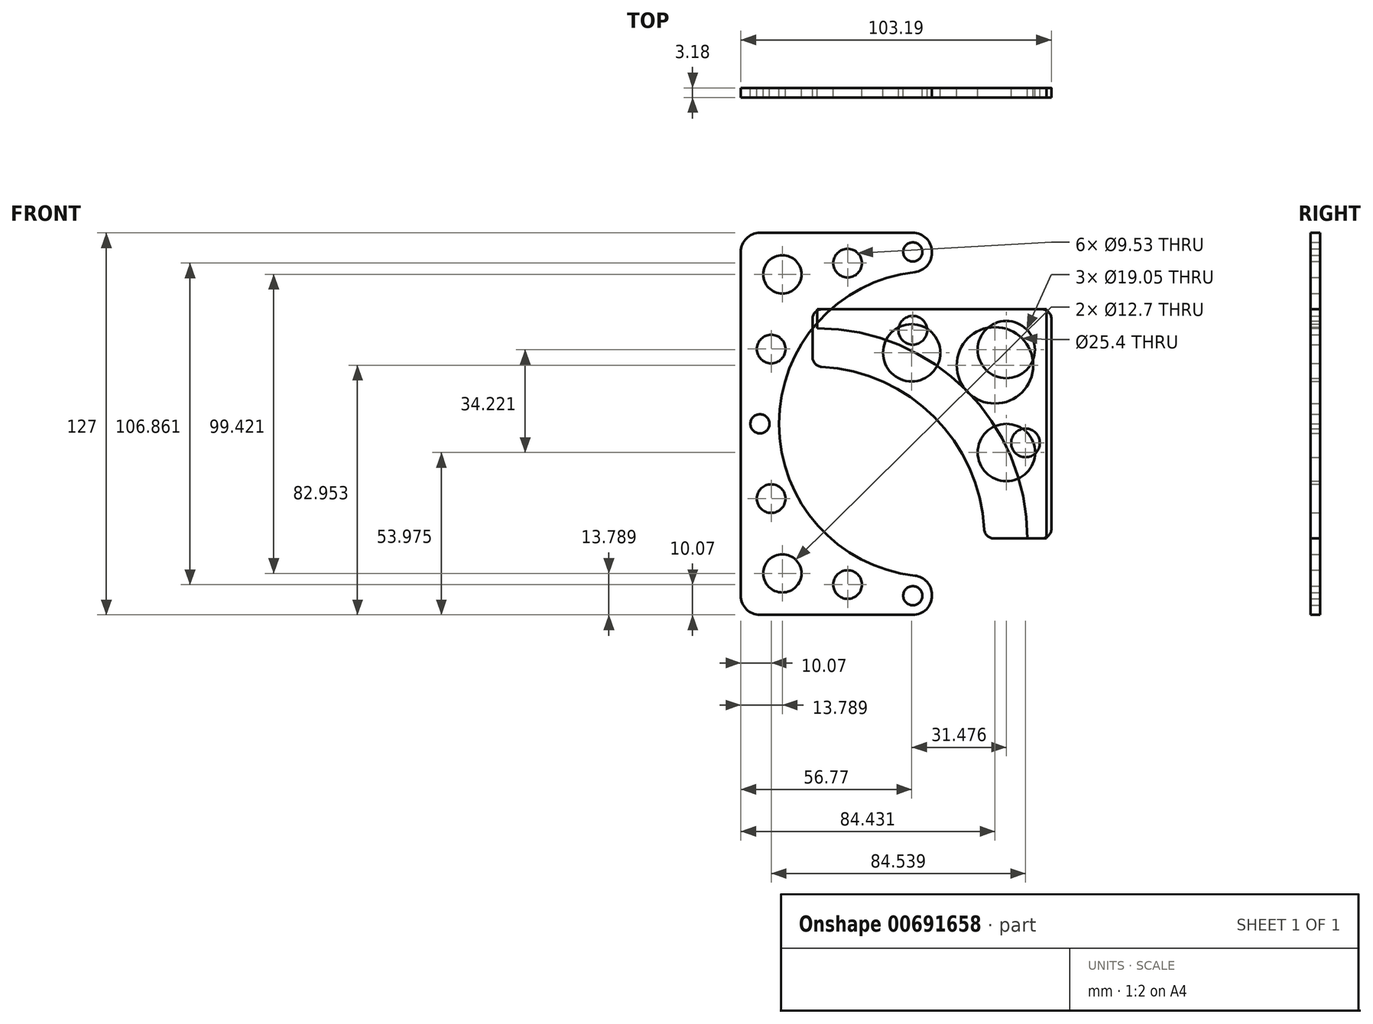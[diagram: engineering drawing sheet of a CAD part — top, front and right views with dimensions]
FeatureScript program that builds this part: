
annotation { "Feature Type Name" : "Feature", "Feature Type Description" : "" }
export const myFeature = defineFeature(function(context is Context, id is Id, definition is map)
    precondition{}
    {
        {
            var Q0;
            Q0=qCreatedBy(makeId("Front.planeOp"),FACE);
            var sketch = newSketch(context, id + "F0", { "sketchPlane" : qUnion([Q0])});
            skLineSegment(sketch, "E0.bottom", {"start": v(38.1, 38.1) * mm, "end": v(-38.1, 38.1) * mm});
            skLineSegment(sketch, "E0.top", {"start": v(38.1, -38.1) * mm, "end": v(31.75, -38.1) * mm});
            skLineSegment(sketch, "E0.left", {"start": v(38.1, 38.1) * mm, "end": v(38.1, -38.1) * mm});
            skLineSegment(sketch, "E0.right", {"start": v(-38.1, 38.1) * mm, "end": v(-38.1, 31.75) * mm});
            skPoint(sketch, "E0.middle", {"position": v(0, 0) * mm});
            skArc(sketch, "E1", {"start": v(31.75, -38.1) * mm, "mid": v(11.3, 11.3) * mm, "end": v(-38.1, 31.75) * mm});
            skCircle(sketch, "E2", {"center": v(24.7, 24.7) * mm, "radius": 9.53 * mm});
            skPoint(sketch, "E3.trimOffspring.end.orphan", {"position": v(11.3, 11.3) * mm});
            skCircle(sketch, "E4", {"center": v(31.1, -6.35) * mm, "radius": 4.76 * mm});
            skPoint(sketch, "E5.trimOffspring.end.orphan", {"position": v(24.12, -6.35) * mm});
            skPoint(sketch, "E6.start.orphan", {"position": v(38.1, -6.35) * mm});
            skLineSegment(sketch, "E7", {"start": v(-38.1, 38.1) * mm, "end": v(-6.35, 38.1) * mm});
            skLineSegment(sketch, "E8", {"start": v(-6.35, 38.1) * mm, "end": v(-6.35, 24.12) * mm});
            skCircle(sketch, "E9", {"center": v(-6.35, 31.1) * mm, "radius": 4.76 * mm});
            skSolve(sketch);
        }
        {
            var Q0;
            Q0 = qSketchRegion(id + "F0", true);
            extrude(context, id + "F1", {"entities" : qUnion([Q0]), "depth" : 3.17 * mm, "offsetDistance" : 25.4 * mm});
        }
        {
            var Q0;
            Q0=qCreatedBy(makeId("Front.planeOp"),FACE);
            var sketch = newSketch(context, id + "F2", { "sketchPlane" : qUnion([Q0])});
            skLineSegment(sketch, "E10.bottom", {"start": v(36.51, 38.1) * mm, "end": v(-36.51, 38.1) * mm});
            skLineSegment(sketch, "E10.top", {"start": v(36.51, -38.1) * mm, "end": v(20.55, -38.1) * mm});
            skLineSegment(sketch, "E10.left", {"start": v(39.69, 34.93) * mm, "end": v(39.69, -34.93) * mm});
            skLineSegment(sketch, "E10.right", {"start": v(-39.69, 34.93) * mm, "end": v(-39.69, 22.14) * mm});
            skPoint(sketch, "E10.middle", {"position": v(0, 0) * mm});
            skArc(sketch, "E11", {"start": v(17.38, -35.1) * mm, "mid": v(0.72, 2.31) * mm, "end": v(-36.68, 18.97) * mm});
            skCircle(sketch, "E12", {"center": v(24.75, -9.53) * mm, "radius": 9.53 * mm});
            skPoint(sketch, "E13.trimOffspring.end.orphan", {"position": v(9.8, -9.53) * mm});
            skPoint(sketch, "E14.end.orphan", {"position": v(39.69, -9.53) * mm});
            skCircle(sketch, "E15", {"center": v(-6.73, 23.6) * mm, "radius": 9.53 * mm});
            skPoint(sketch, "E16.trimOffspring.end.orphan", {"position": v(-7.49, 9.12) * mm});
            skPoint(sketch, "E17.end.orphan", {"position": v(-5.97, 38.1) * mm});
            skCircle(sketch, "E18", {"center": v(20.93, 19.45) * mm, "radius": 12.7 * mm});
            skPoint(sketch, "E19.trimOffspring.end.orphan", {"position": v(2.17, 0.8) * mm});
            skPoint(sketch, "E20.visualSharp", {"position": v(39.69, 38.1) * mm});
            skArc(sketch, "E20.filletArc", {"start": v(39.69, 34.93) * mm, "mid": v(38.76, 37.17) * mm, "end": v(36.51, 38.1) * mm});
            skPoint(sketch, "E21.visualSharp", {"position": v(39.69, -38.1) * mm});
            skArc(sketch, "E21.filletArc", {"start": v(36.51, -38.1) * mm, "mid": v(38.76, -37.17) * mm, "end": v(39.69, -34.93) * mm});
            skPoint(sketch, "E22.visualSharp", {"position": v(17.46, -38.1) * mm});
            skArc(sketch, "E22.filletArc", {"start": v(17.38, -35.1) * mm, "mid": v(18.37, -37.23) * mm, "end": v(20.55, -38.1) * mm});
            skPoint(sketch, "E23.visualSharp", {"position": v(-39.69, 19.05) * mm});
            skArc(sketch, "E23.filletArc", {"start": v(-39.69, 22.14) * mm, "mid": v(-38.82, 19.96) * mm, "end": v(-36.68, 18.97) * mm});
            skPoint(sketch, "E24.visualSharp", {"position": v(-39.69, 38.1) * mm});
            skArc(sketch, "E24.filletArc", {"start": v(-36.51, 38.1) * mm, "mid": v(-38.76, 37.17) * mm, "end": v(-39.69, 34.93) * mm});
            skSolve(sketch);
        }
        {
            var Q0;
            Q0 = qSketchRegion(id + "F2", true);
            extrude(context, id + "F3", {"entities" : qUnion([Q0]), "depth" : 3.17 * mm, "offsetDistance" : 25.4 * mm});
        }
        {
            var Q0;
            Q0=qCreatedBy(makeId("Front.planeOp"),FACE);
            var sketch = newSketch(context, id + "F4", { "sketchPlane" : qUnion([Q0])});
            skLineSegment(sketch, "E25.bottom", {"start": v(-6.35, 63.5) * mm, "end": v(-57.15, 63.5) * mm});
            skLineSegment(sketch, "E25.top", {"start": v(-6.35, -63.5) * mm, "end": v(-57.15, -63.5) * mm});
            skLineSegment(sketch, "E25.right", {"start": v(-63.5, 57.15) * mm, "end": v(-63.5, -57.15) * mm});
            skPoint(sketch, "E25.middle", {"position": v(0, 0) * mm});
            skArc(sketch, "E26", {"start": v(-5.64, 50.49) * mm, "mid": v(-50.8, 0) * mm, "end": v(-5.64, -50.49) * mm});
            skLineSegment(sketch, "E27", {"start": v(0, 57.15) * mm, "end": v(0, 56.8) * mm});
            skPoint(sketch, "E28.orphan", {"position": v(63.5, -63.5) * mm});
            skPoint(sketch, "E25.left.end.orphan", {"position": v(63.5, 0) * mm});
            skPoint(sketch, "E29.orphan", {"position": v(63.5, 63.5) * mm});
            skLineSegment(sketch, "E30.trimOffspring", {"start": v(0, -56.8) * mm, "end": v(0, -57.15) * mm});
            skPoint(sketch, "E31.visualSharp", {"position": v(0, 63.5) * mm});
            skArc(sketch, "E31.filletArc", {"start": v(0, 57.15) * mm, "mid": v(-1.86, 61.64) * mm, "end": v(-6.35, 63.5) * mm});
            skPoint(sketch, "E32.visualSharp", {"position": v(0, 50.8) * mm});
            skArc(sketch, "E32.filletArc", {"start": v(-5.64, 50.49) * mm, "mid": v(-1.62, 52.56) * mm, "end": v(0, 56.8) * mm});
            skPoint(sketch, "E33.visualSharp", {"position": v(-63.5, 63.5) * mm});
            skArc(sketch, "E33.filletArc", {"start": v(-57.15, 63.5) * mm, "mid": v(-61.64, 61.64) * mm, "end": v(-63.5, 57.15) * mm});
            skPoint(sketch, "E34.visualSharp", {"position": v(0, -50.8) * mm});
            skArc(sketch, "E34.filletArc", {"start": v(0, -56.8) * mm, "mid": v(-1.62, -52.56) * mm, "end": v(-5.64, -50.49) * mm});
            skPoint(sketch, "E35.visualSharp", {"position": v(0, -63.5) * mm});
            skArc(sketch, "E35.filletArc", {"start": v(-6.35, -63.5) * mm, "mid": v(-1.86, -61.64) * mm, "end": v(0, -57.15) * mm});
            skPoint(sketch, "E36.visualSharp", {"position": v(-63.5, -63.5) * mm});
            skArc(sketch, "E36.filletArc", {"start": v(-63.5, -57.15) * mm, "mid": v(-61.64, -61.64) * mm, "end": v(-57.15, -63.5) * mm});
            skLineSegment(sketch, "E37", {"start": v(-63.5, 63.5) * mm, "end": v(-61.64, 61.64) * mm});
            skLineSegment(sketch, "E38", {"start": v(-63.5, -63.5) * mm, "end": v(-61.64, -61.64) * mm});
            skCircle(sketch, "E39", {"center": v(-49.71, 49.71) * mm, "radius": 6.35 * mm});
            skCircle(sketch, "E40", {"center": v(-49.71, -49.71) * mm, "radius": 6.35 * mm});
            skPoint(sketch, "E41.trimOffspring.end.orphan", {"position": v(-35.92, 35.92) * mm});
            skPoint(sketch, "E42.orphan", {"position": v(-35.92, -35.92) * mm});
            skCircle(sketch, "E43", {"center": v(-57.15, 0) * mm, "radius": 3.18 * mm});
            skPoint(sketch, "E44.trimOffspring.end.orphan", {"position": v(-63.5, 0) * mm});
            skPoint(sketch, "E45.start.orphan", {"position": v(-50.8, 0) * mm});
            skCircle(sketch, "E46", {"center": v(-53.43, 24.86) * mm, "radius": 4.76 * mm});
            skCircle(sketch, "E47", {"center": v(-53.43, -24.86) * mm, "radius": 4.76 * mm});
            skCircle(sketch, "E48", {"center": v(-6.35, 57.15) * mm, "radius": 3.18 * mm});
            skCircle(sketch, "E49", {"center": v(-28.03, 53.43) * mm, "radius": 4.76 * mm});
            skCircle(sketch, "E50", {"center": v(-6.35, -57.15) * mm, "radius": 3.18 * mm});
            skCircle(sketch, "E51", {"center": v(-28.03, -53.43) * mm, "radius": 4.76 * mm});
            skSolve(sketch);
        }
        {
            var Q0;
            Q0 = qSketchRegion(id + "F4", true);
            extrude(context, id + "F5", {"entities" : qUnion([Q0]), "depth" : 3.17 * mm, "offsetDistance" : 25.4 * mm});
        }
    });
